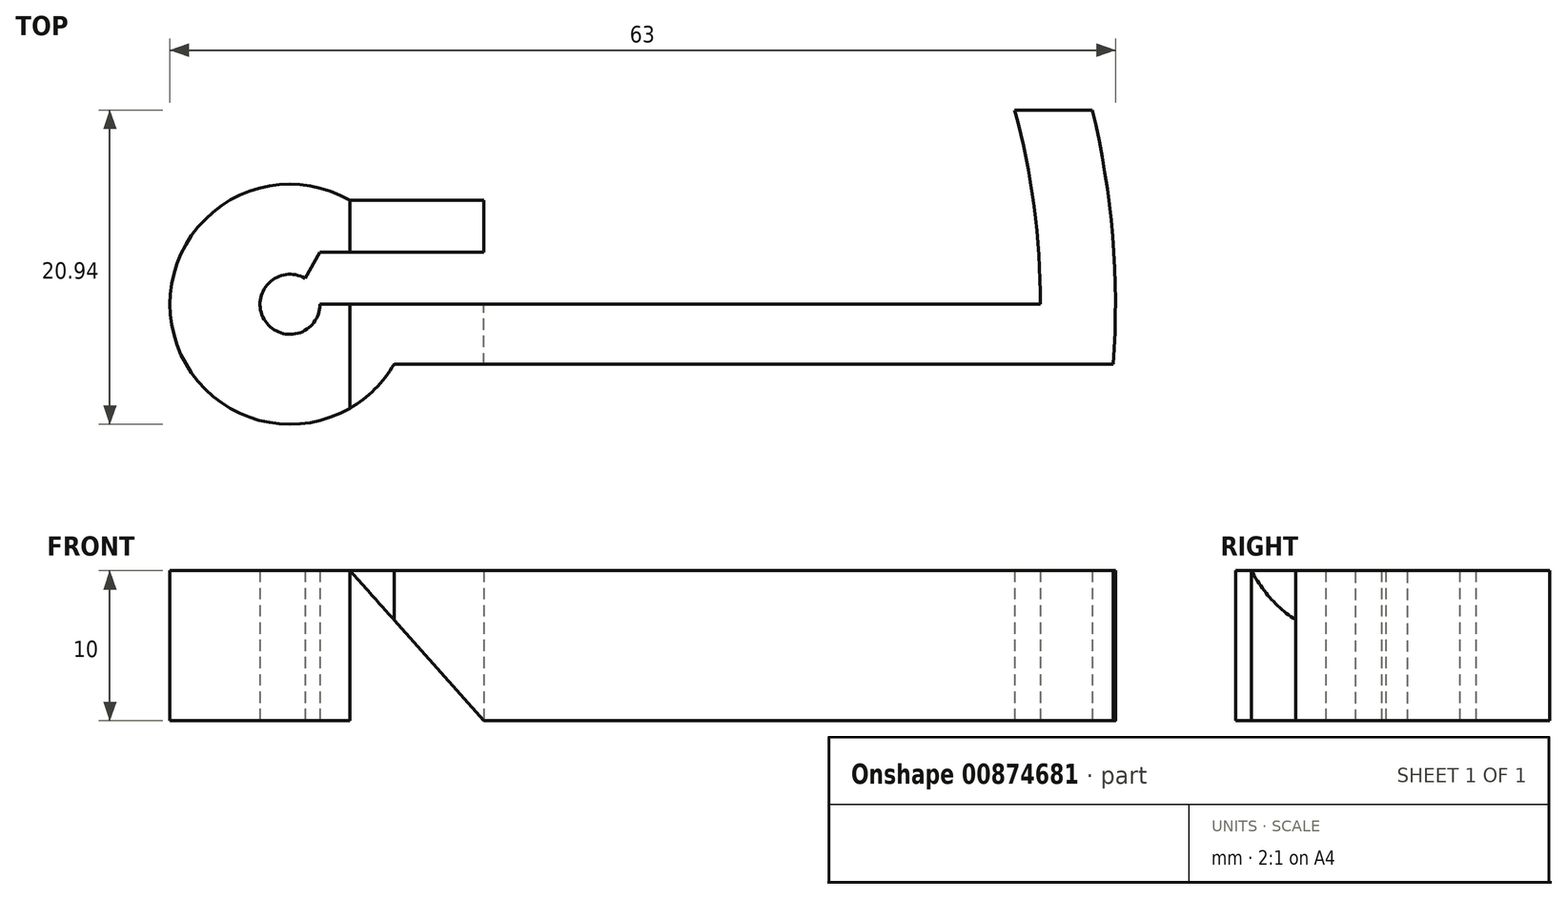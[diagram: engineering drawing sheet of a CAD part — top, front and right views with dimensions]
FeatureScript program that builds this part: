
annotation { "Feature Type Name" : "Feature", "Feature Type Description" : "" }
export const myFeature = defineFeature(function(context is Context, id is Id, definition is map)
    precondition{}
    {
        {
            var Q0;
            Q0=qCreatedBy(makeId("Top.planeOp"),FACE);
            var sketch = newSketch(context, id + "F0", { "sketchPlane" : qUnion([Q0])});
            skCircle(sketch, "E0", {"center": v(0, 0) * mm, "radius": 2 * mm});
            skCircle(sketch, "E1", {"center": v(0, 0) * mm, "radius": 8 * mm});
            skCircle(sketch, "E2", {"center": v(0, 0) * mm, "radius": 55 * mm});
            skCircle(sketch, "E3", {"center": v(0, 0) * mm, "radius": 50 * mm});
            skLineSegment(sketch, "E4", {"start": v(2, 0) * mm, "end": v(8, 0) * mm});
            skLineSegment(sketch, "E5", {"start": v(0, 0) * mm, "end": v(55, 0) * mm});
            skLineSegment(sketch, "E6", {"start": v(0, -4) * mm, "end": v(54.85, -4) * mm});
            skLineSegment(sketch, "E7", {"start": v(0, 0) * mm, "end": v(4, 6.93) * mm});
            skLineSegment(sketch, "E8", {"start": v(0, 0) * mm, "end": v(53.13, 14.24) * mm});
            skPoint(sketch, "E9", {"position": v(48.3, 12.94) * mm});
            skLineSegment(sketch, "E10", {"start": v(2, 3.46) * mm, "end": v(12.93, 3.46) * mm});
            skLineSegment(sketch, "E11", {"start": v(4, 6.93) * mm, "end": v(12.93, 6.93) * mm});
            skLineSegment(sketch, "E12", {"start": v(12.93, 6.93) * mm, "end": v(12.93, 3.46) * mm});
            skLineSegment(sketch, "E13", {"start": v(48.3, 12.94) * mm, "end": v(53.46, 12.94) * mm});
            skSolve(sketch);
        }
        {
            var Q0;
            {var subQ1=sQuery(id+"F0.wireOp",EDGE,"E4");Q0=makeQuery(id+"F0.imprint","IMPRINT",FACE,{"disambiguationData":[TD([[makeQuery(id+"F0.imprint","IMPRINT",EDGE,{"derivedFrom":subQ1}),-1.0]])]});}
            var Q1;
            {var subQ0=sQuery(id+"F0.wireOp",EDGE,"E5");var subQ5=sQuery(id+"F0.wireOp",EDGE,"E3");var subQ6=makeQuery(id+"F0.imprint","INTERSECT",VERTEX,{"derivedFrom":[subQ5,subQ0]});Q1=makeQuery(id+"F0.imprint","IMPRINT",FACE,{"disambiguationData":[TD([[makeQuery(id+"F0.imprint","IMPRINT",EDGE,{"disambiguationData":[TD([[subQ6,1.0]])],"derivedFrom":subQ5}),1.0]])]});}
            var Q2;
            {var subQ0=sQuery(id+"F0.wireOp",EDGE,"E6");var subQ1=sQuery(id+"F0.wireOp",EDGE,"E2");var subQ2=makeQuery(id+"F0.imprint","INTERSECT",VERTEX,{"derivedFrom":[subQ1,subQ0]});Q2=makeQuery(id+"F0.imprint","IMPRINT",FACE,{"disambiguationData":[TD([[makeQuery(id+"F0.imprint","IMPRINT",EDGE,{"disambiguationData":[TD([[subQ2,-1.0]])],"derivedFrom":subQ1}),1.0]])]});}
            var Q3;
            {var subQ0=sQuery(id+"F0.wireOp",EDGE,"E11");Q3=makeQuery(id+"F0.imprint","IMPRINT",FACE,{"disambiguationData":[TD([[makeQuery(id+"F0.imprint","IMPRINT",EDGE,{"derivedFrom":subQ0}),-1.0]])]});}
            var Q4;
            {var subQ1=sQuery(id+"F0.wireOp",EDGE,"E1");var subQ3=sQuery(id+"F0.wireOp",EDGE,"E10");var subQ4=makeQuery(id+"F0.imprint","INTERSECT",VERTEX,{"derivedFrom":[subQ1,subQ3]});Q4=makeQuery(id+"F0.imprint","IMPRINT",FACE,{"disambiguationData":[TD([[makeQuery(id+"F0.imprint","IMPRINT",EDGE,{"disambiguationData":[TD([[subQ4,-1.0]])],"derivedFrom":subQ1}),1.0]])]});}
            var Q5;
            {var subQ0=sQuery(id+"F0.wireOp",EDGE,"E13");Q5=makeQuery(id+"F0.imprint","IMPRINT",FACE,{"disambiguationData":[TD([[makeQuery(id+"F0.imprint","IMPRINT",EDGE,{"derivedFrom":subQ0}),-1.0]])]});}
            extrude(context, id + "F1", {"entities" : qUnion([Q0, Q1, Q2, Q3, Q4, Q5]), "depth" : 10 * mm, "offsetDistance" : 25 * mm});
        }
        {
            var Q0;
            Q0=makeQuery(id+"F1.opExtrude","SWEPT_FACE",FACE,{"disambiguationData":[OSD([sQuery(id+"F0.wireOp",EDGE,"E11")])]});
            var sketch = newSketch(context, id + "F2", { "sketchPlane" : qUnion([Q0])});
            skLineSegment(sketch, "E14", {"start": v(-12.93, 10) * mm, "end": v(-4, 0) * mm});
            skLineSegment(sketch, "E15", {"start": v(-4, 0) * mm, "end": v(-12.93, 0) * mm});
            skLineSegment(sketch, "E16", {"start": v(-12.93, 0) * mm, "end": v(-4, 10) * mm});
            skCircle(sketch, "E17", {"center": v(-8.46, 5) * mm, "radius": 1.5 * mm});
            skSolve(sketch);
        }
        {
            var Q0;
            {var subQ0=sQuery(id+"F2.wireOp",EDGE,"E16");var subQ1=sQuery(id+"F2.wireOp",EDGE,"E14");var subQ2=makeQuery(id+"F2.imprint","INTERSECT",VERTEX,{"derivedFrom":[subQ1,subQ0]});Q0=makeQuery(id+"F2.imprint","IMPRINT",FACE,{"disambiguationData":[TD([[makeQuery(id+"F2.imprint","IMPRINT",EDGE,{"disambiguationData":[TD([[subQ2,-1.0]])],"derivedFrom":subQ1}),1.0]])]});}
            var Q1;
            {var subQ0=sQuery(id+"F2.wireOp",EDGE,"E16");var subQ1=sQuery(id+"F2.wireOp",EDGE,"E14");var subQ2=makeQuery(id+"F2.imprint","INTERSECT",VERTEX,{"derivedFrom":[subQ1,subQ0]});Q1=makeQuery(id+"F2.imprint","IMPRINT",FACE,{"disambiguationData":[TD([[makeQuery(id+"F2.imprint","IMPRINT",EDGE,{"disambiguationData":[TD([[subQ2,-1.0]])],"derivedFrom":subQ1}),-1.0]])]});}
            var Q2;
            {var subQ0=sQuery(id+"F2.wireOp",EDGE,"E17");var subQ1=sQuery(id+"F2.wireOp",EDGE,"E14");var subQ2=makeQuery(id+"F2.imprint","INTERSECT",VERTEX,{"disambiguationData":[OD(0.0)],"derivedFrom":[subQ1,subQ0]});Q2=makeQuery(id+"F2.imprint","IMPRINT",FACE,{"disambiguationData":[TD([[makeQuery(id+"F2.imprint","IMPRINT",EDGE,{"disambiguationData":[TD([[subQ2,-1.0]])],"derivedFrom":subQ1}),-1.0]])]});}
            var Q3;
            {var subQ0=sQuery(id+"F2.wireOp",EDGE,"E17");var subQ1=sQuery(id+"F2.wireOp",EDGE,"E14");var subQ2=makeQuery(id+"F2.imprint","INTERSECT",VERTEX,{"disambiguationData":[OD(0.0)],"derivedFrom":[subQ1,subQ0]});Q3=makeQuery(id+"F2.imprint","IMPRINT",FACE,{"disambiguationData":[TD([[makeQuery(id+"F2.imprint","IMPRINT",EDGE,{"disambiguationData":[TD([[subQ2,-1.0]])],"derivedFrom":subQ1}),1.0]])]});}
            extrude(context, id + "F3", {"entities" : qUnion([Q0, Q1, Q2, Q3]), "operationType" : NewBodyOperationType.REMOVE, "oppositeDirection" : true, "depth" : 25 * mm, "offsetDistance" : 25 * mm});
        }
    });
